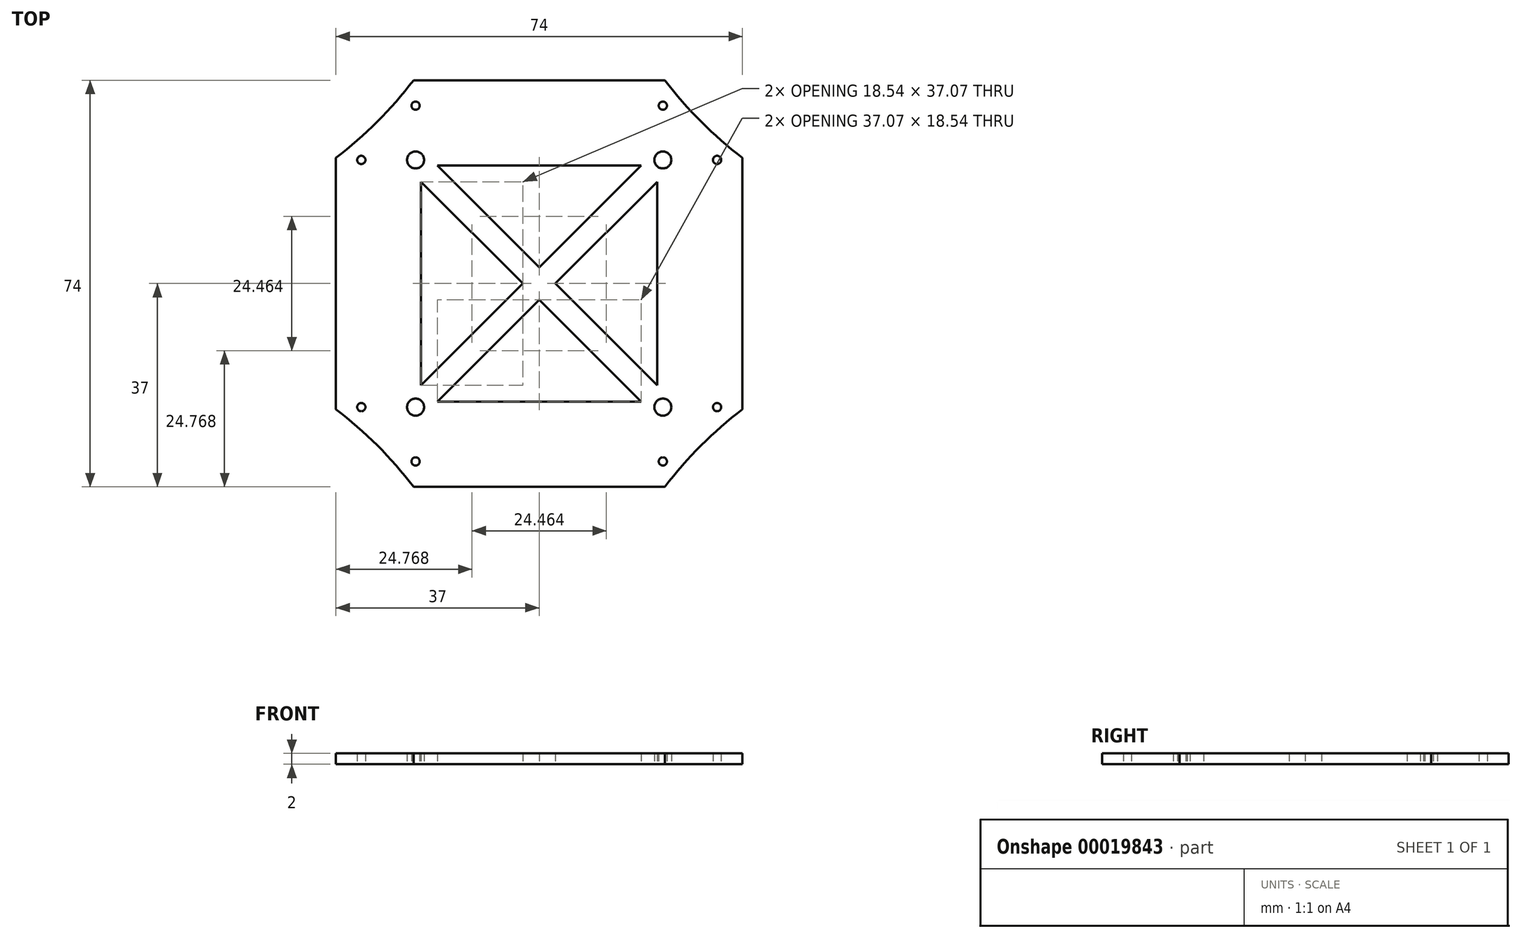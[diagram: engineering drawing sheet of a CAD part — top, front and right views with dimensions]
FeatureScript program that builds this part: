
annotation { "Feature Type Name" : "Feature", "Feature Type Description" : "" }
export const myFeature = defineFeature(function(context is Context, id is Id, definition is map)
    precondition{}
    {
        {
            var Q0;
            Q0=qCreatedBy(makeId("Top.planeOp"),FACE);
            var sketch = newSketch(context, id + "F0", { "sketchPlane" : qUnion([Q0])});
            skLineSegment(sketch, "E0.rect.bottom", {"start": v(27, -27) * mm, "end": v(-27, -27) * mm});
            skLineSegment(sketch, "E0.rect.top", {"start": v(27, 27) * mm, "end": v(-27, 27) * mm});
            skLineSegment(sketch, "E0.rect.left", {"start": v(27, -27) * mm, "end": v(27, 27) * mm});
            skLineSegment(sketch, "E0.rect.right", {"start": v(-27, -27) * mm, "end": v(-27, 27) * mm});
            skPoint(sketch, "E0.rect.middle", {"position": v(0, 0) * mm});
            skCircle(sketch, "E1", {"center": v(-22.5, 22.5) * mm, "radius": 1.55 * mm});
            skLineSegment(sketch, "E2", {"start": v(0, 32.48) * mm, "end": v(0, -34.77) * mm, "construction": true});
            skLineSegment(sketch, "E3", {"start": v(-38.82, 0) * mm, "end": v(33.89, 0) * mm, "construction": true});
            skCircle(sketch, "E4.MirrorC", {"center": v(22.5, 22.5) * mm, "radius": 1.55 * mm});
            skCircle(sketch, "E5.MirrorC", {"center": v(22.5, -22.5) * mm, "radius": 1.55 * mm});
            skCircle(sketch, "E6.MirrorC", {"center": v(-22.5, -22.5) * mm, "radius": 1.55 * mm});
            skLineSegment(sketch, "E7", {"start": v(20.95, 22.5) * mm, "end": v(-20.95, 22.5) * mm, "construction": true});
            skLineSegment(sketch, "E8", {"start": v(-20.95, 22.5) * mm, "end": v(0, 1.55) * mm, "construction": true});
            skLineSegment(sketch, "E9", {"start": v(0, 1.55) * mm, "end": v(20.95, 22.5) * mm, "construction": true});
            skLineSegment(sketch, "E10.0", {"start": v(-18.54, 21.5) * mm, "end": v(0, 2.96) * mm});
            skLineSegment(sketch, "E10.1", {"start": v(18.54, 21.5) * mm, "end": v(-18.54, 21.5) * mm});
            skLineSegment(sketch, "E10.2", {"start": v(0, 2.96) * mm, "end": v(18.54, 21.5) * mm});
            skLineSegment(sketch, "E11.1.0", {"start": v(-21.5, -18.54) * mm, "end": v(-2.96, 0) * mm});
            skLineSegment(sketch, "E11.1.1", {"start": v(-2.96, 0) * mm, "end": v(-21.5, 18.54) * mm});
            skLineSegment(sketch, "E11.1.2", {"start": v(-21.5, 18.54) * mm, "end": v(-21.5, -18.54) * mm});
            skLineSegment(sketch, "E11.2.0", {"start": v(18.54, -21.5) * mm, "end": v(0, -2.96) * mm});
            skLineSegment(sketch, "E11.2.1", {"start": v(0, -2.96) * mm, "end": v(-18.54, -21.5) * mm});
            skLineSegment(sketch, "E11.2.2", {"start": v(-18.54, -21.5) * mm, "end": v(18.54, -21.5) * mm});
            skLineSegment(sketch, "E12.1.3.0", {"start": v(21.5, 18.54) * mm, "end": v(2.96, 0) * mm});
            skLineSegment(sketch, "E12.3.3.0", {"start": v(2.96, 0) * mm, "end": v(21.5, -18.54) * mm});
            skLineSegment(sketch, "E12.6.3.0", {"start": v(21.5, -18.54) * mm, "end": v(21.5, 18.54) * mm});
            skLineSegment(sketch, "E13.rect.bottom", {"start": v(22.5, -22.5) * mm, "end": v(-22.5, -22.5) * mm, "construction": true});
            skLineSegment(sketch, "E13.rect.top", {"start": v(22.5, 22.5) * mm, "end": v(-22.5, 22.5) * mm, "construction": true});
            skLineSegment(sketch, "E13.rect.left", {"start": v(22.5, -22.5) * mm, "end": v(22.5, 22.5) * mm, "construction": true});
            skLineSegment(sketch, "E13.rect.right", {"start": v(-22.5, -22.5) * mm, "end": v(-22.5, 22.5) * mm, "construction": true});
            skLineSegment(sketch, "E14.rect.bottom", {"start": v(32.37, 32.38) * mm, "end": v(-32.38, 32.37) * mm, "construction": true});
            skLineSegment(sketch, "E14.rect.top", {"start": v(32.38, -32.37) * mm, "end": v(-32.37, -32.37) * mm, "construction": true});
            skLineSegment(sketch, "E14.rect.left", {"start": v(32.37, 32.38) * mm, "end": v(32.37, -32.37) * mm, "construction": true});
            skLineSegment(sketch, "E14.rect.right", {"start": v(-32.38, 32.37) * mm, "end": v(-32.37, -32.37) * mm, "construction": true});
            skLineSegment(sketch, "E15.rect.bottom", {"start": v(37, -37) * mm, "end": v(-37, -37) * mm});
            skLineSegment(sketch, "E15.rect.top", {"start": v(37, 37) * mm, "end": v(-37, 37) * mm});
            skLineSegment(sketch, "E15.rect.left", {"start": v(37, -37) * mm, "end": v(37, 37) * mm});
            skLineSegment(sketch, "E15.rect.right", {"start": v(-37, -37) * mm, "end": v(-37, 37) * mm});
            skCircle(sketch, "E16", {"center": v(-32.37, 22.5) * mm, "radius": 0.75 * mm});
            skCircle(sketch, "E17", {"center": v(32.37, 22.5) * mm, "radius": 0.75 * mm});
            skCircle(sketch, "E18.MirrorC", {"center": v(32.37, -22.5) * mm, "radius": 0.75 * mm});
            skCircle(sketch, "E19.MirrorC", {"center": v(-32.37, -22.5) * mm, "radius": 0.75 * mm});
            skLineSegment(sketch, "E20", {"start": v(-37, 37) * mm, "end": v(37, -37) * mm, "construction": true});
            skLineSegment(sketch, "E21", {"start": v(37, 37) * mm, "end": v(-37, -37) * mm, "construction": true});
            skCircle(sketch, "E22.MirrorC", {"center": v(-22.5, 32.37) * mm, "radius": 0.75 * mm});
            skCircle(sketch, "E23.MirrorC", {"center": v(22.5, -32.37) * mm, "radius": 0.75 * mm});
            skCircle(sketch, "E24.MirrorC", {"center": v(22.5, 32.37) * mm, "radius": 0.75 * mm});
            skCircle(sketch, "E25.MirrorC", {"center": v(-22.5, -32.37) * mm, "radius": 0.75 * mm});
            skLineSegment(sketch, "E26.rect.bottom", {"start": v(-82.5, -82.5) * mm, "end": v(82.5, -82.5) * mm, "construction": true});
            skLineSegment(sketch, "E26.rect.top", {"start": v(-82.5, 82.5) * mm, "end": v(82.5, 82.5) * mm, "construction": true});
            skLineSegment(sketch, "E26.rect.left", {"start": v(-82.5, -82.5) * mm, "end": v(-82.5, 82.5) * mm, "construction": true});
            skLineSegment(sketch, "E26.rect.right", {"start": v(82.5, -82.5) * mm, "end": v(82.5, 82.5) * mm, "construction": true});
            skCircle(sketch, "E27", {"center": v(-82.5, 82.5) * mm, "radius": 75 * mm});
            skCircle(sketch, "E28.1.1", {"center": v(-82.5, -82.5) * mm, "radius": 75 * mm});
            skCircle(sketch, "E28.2.1", {"center": v(82.5, -82.5) * mm, "radius": 75 * mm});
            skCircle(sketch, "E28.3.1", {"center": v(82.5, 82.5) * mm, "radius": 75 * mm});
            skSolve(sketch);
        }
        {
            var Q0;
            Q0=makeQuery(id+"F0.imprint","IMPRINT",FACE,{"disambiguationData":[TD([[makeQuery(id+"F0.imprint","IMPRINT",EDGE,{"derivedFrom":sQuery(id+"F0.wireOp",EDGE,"E0.rect.bottom")}),1.0]])]});
            var Q1;
            Q1=makeQuery(id+"F0.imprint","IMPRINT",FACE,{"disambiguationData":[TD([[makeQuery(id+"F0.imprint","IMPRINT",EDGE,{"derivedFrom":sQuery(id+"F0.wireOp",EDGE,"E0.rect.bottom")}),-1.0]])]});
            extrude(context, id + "F1", {"entities" : qUnion([Q0, Q1]), "depth" : 2 * mm});
        }
    });
